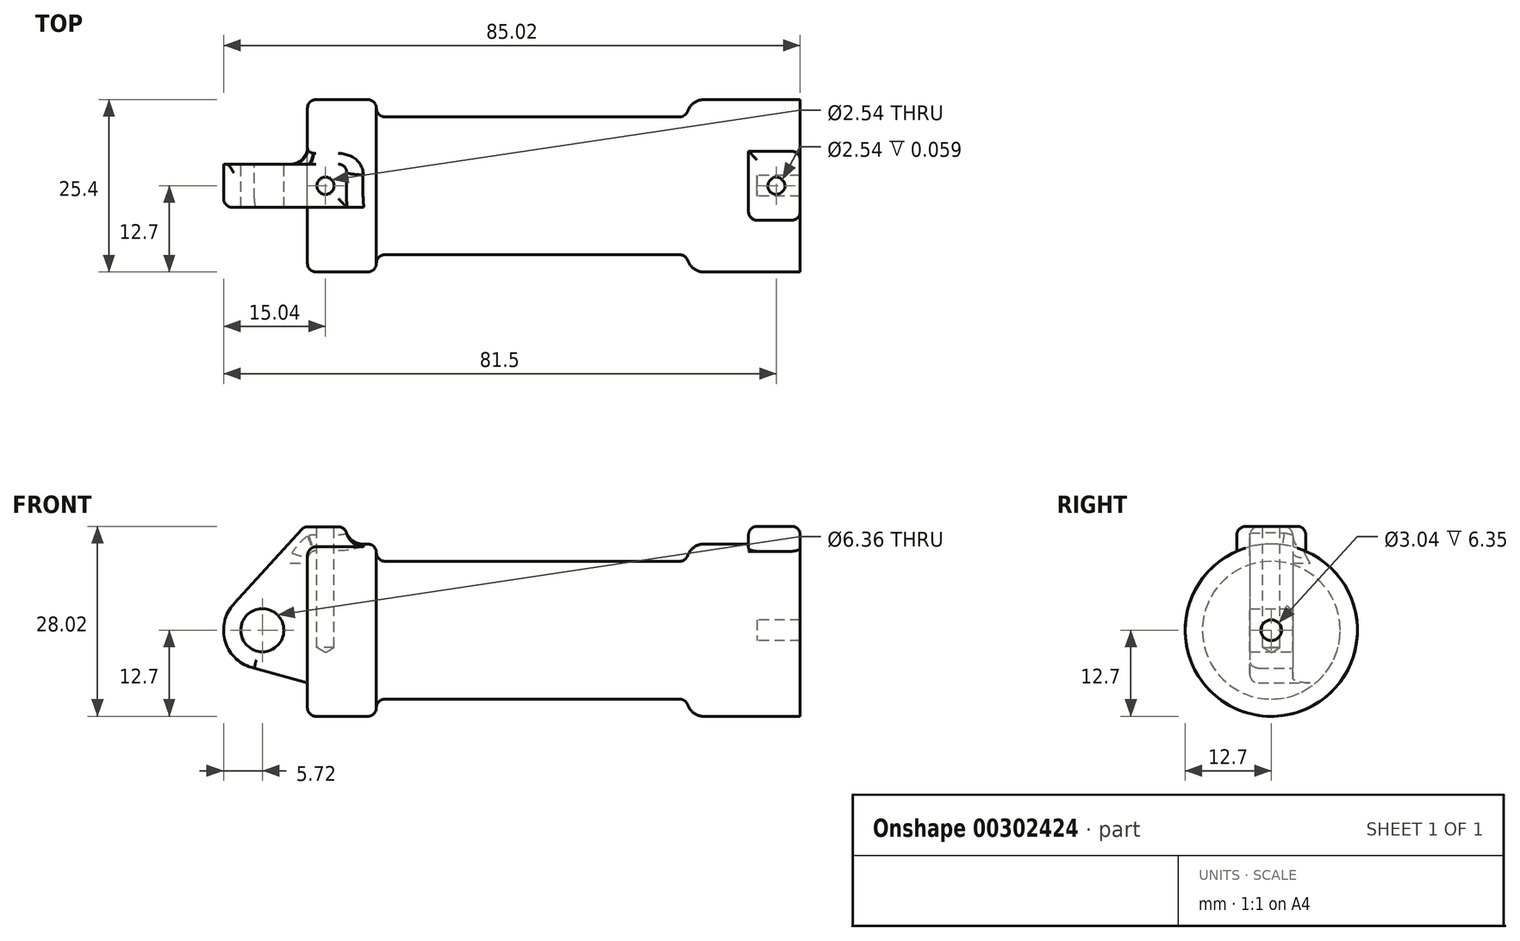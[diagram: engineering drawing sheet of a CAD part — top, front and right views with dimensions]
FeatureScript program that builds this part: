
annotation { "Feature Type Name" : "Feature", "Feature Type Description" : "" }
export const myFeature = defineFeature(function(context is Context, id is Id, definition is map)
    precondition{}
    {
        {
            var Q0;
            Q0=qCreatedBy(makeId("Front.planeOp"),FACE);
            var sketch = newSketch(context, id + "F0", { "sketchPlane" : qUnion([Q0])});
            skLineSegment(sketch, "E0", {"start": v(0, 0) * mm, "end": v(0, 12.7) * mm});
            skLineSegment(sketch, "E1", {"start": v(0, 12.7) * mm, "end": v(10.16, 12.7) * mm});
            skLineSegment(sketch, "E2", {"start": v(10.16, 12.7) * mm, "end": v(10.16, 10.16) * mm});
            skLineSegment(sketch, "E3", {"start": v(10.16, 10.16) * mm, "end": v(56.13, 10.16) * mm});
            skLineSegment(sketch, "E4", {"start": v(56.13, 10.16) * mm, "end": v(56.13, 12.7) * mm});
            skLineSegment(sketch, "E5", {"start": v(56.13, 12.7) * mm, "end": v(66.3, 12.7) * mm});
            skLineSegment(sketch, "E6", {"start": v(66.3, 12.7) * mm, "end": v(66.3, 0) * mm});
            skLineSegment(sketch, "E7", {"start": v(66.3, 0) * mm, "end": v(0, 0) * mm});
            skLineSegment(sketch, "E8", {"start": v(5.84, 15.24) * mm, "end": v(-0.5, 15.24) * mm});
            skLineSegment(sketch, "E9", {"start": v(-0.5, 15.24) * mm, "end": v(-10.88, 3.85) * mm});
            skLineSegment(sketch, "E10", {"start": v(0, 0) * mm, "end": v(-6.65, 0) * mm});
            skCircle(sketch, "E11", {"center": v(-6.65, 0) * mm, "radius": 5.72 * mm});
            skCircle(sketch, "E12", {"center": v(-6.65, 0) * mm, "radius": 3.18 * mm});
            skLineSegment(sketch, "E13", {"start": v(5.84, 15.24) * mm, "end": v(5.84, -9.4) * mm});
            skLineSegment(sketch, "E14", {"start": v(5.84, -9.4) * mm, "end": v(-8.18, -5.5) * mm});
            skSolve(sketch);
        }
        {
            var Q0;
            {var subQ0=sQuery(id+"F0.wireOp",EDGE,"E2");Q0=makeQuery(id+"F0.imprint","IMPRINT",FACE,{"disambiguationData":[TD([[makeQuery(id+"F0.imprint","IMPRINT",EDGE,{"derivedFrom":subQ0}),-1.0]])]});}
            var Q1;
            {var subQ0=sQuery(id+"F0.wireOp",EDGE,"E0");Q1=makeQuery(id+"F0.imprint","IMPRINT",FACE,{"disambiguationData":[TD([[makeQuery(id+"F0.imprint","IMPRINT",EDGE,{"derivedFrom":subQ0}),-1.0]])]});}
            var Q2;
            Q2=sQuery(id+"F0.wireOp",EDGE,"E7");
            revolve(context, id + "F1", {"entities" : qUnion([Q0, Q1]), "axis" : qUnion([Q2]), "revolveType" : RevolveType.FULL});
        }
        {
            var Q0;
            {var subQ1=sQuery(id+"F0.wireOp",EDGE,"E0");Q0=makeQuery(id+"F0.imprint","IMPRINT",FACE,{"disambiguationData":[TD([[makeQuery(id+"F0.imprint","IMPRINT",EDGE,{"derivedFrom":subQ1}),1.0]])]});}
            var Q1;
            {var subQ0=sQuery(id+"F0.wireOp",EDGE,"E14");Q1=makeQuery(id+"F0.imprint","IMPRINT",FACE,{"disambiguationData":[TD([[makeQuery(id+"F0.imprint","IMPRINT",EDGE,{"derivedFrom":subQ0}),-1.0]])]});}
            var Q2;
            {var subQ5=sQuery(id+"F0.wireOp",EDGE,"E12");Q2=makeQuery(id+"F0.imprint","IMPRINT",FACE,{"disambiguationData":[TD([[makeQuery(id+"F0.imprint","IMPRINT",EDGE,{"derivedFrom":subQ5}),-1.0]])]});}
            var Q3;
            {var subQ0=sQuery(id+"F0.wireOp",EDGE,"E0");Q3=makeQuery(id+"F0.imprint","IMPRINT",FACE,{"disambiguationData":[TD([[makeQuery(id+"F0.imprint","IMPRINT",EDGE,{"derivedFrom":subQ0}),-1.0]])]});}
            extrude(context, id + "F2", {"entities" : qUnion([Q0, Q1, Q2, Q3]), "operationType" : NewBodyOperationType.ADD, "depth" : 6.35 * mm, "symmetric" : true});
        }
        {
            var Q0;
            Q0=makeQuery(id+"F1.opRevolve","SWEPT_FACE",FACE,{"disambiguationData":[OSD([sQuery(id+"F0.wireOp",EDGE,"E6")])]});
            var sketch = newSketch(context, id + "F3", { "sketchPlane" : qUnion([Q0])});
            skCircle(sketch, "E15", {"center": v(0, 0) * mm, "radius": 5.08 * mm});
            skCircle(sketch, "E16", {"center": v(0, 0) * mm, "radius": 1.52 * mm});
            skLineSegment(sketch, "E17", {"start": v(-5.08, 0.16) * mm, "end": v(-5.08, 15.28) * mm});
            skLineSegment(sketch, "E18", {"start": v(5.08, 0) * mm, "end": v(5.08, 15.33) * mm});
            skLineSegment(sketch, "E19", {"start": v(5.08, 15.33) * mm, "end": v(-5.08, 15.28) * mm});
            skSolve(sketch);
        }
        {
            var Q0;
            {var subQ0=sQuery(id+"F3.wireOp",EDGE,"E19");Q0=makeQuery(id+"F3.imprint","IMPRINT",FACE,{"disambiguationData":[TD([[makeQuery(id+"F3.imprint","IMPRINT",EDGE,{"derivedFrom":subQ0}),1.0]])]});}
            var Q1;
            {var subQ0=sQuery(id+"F3.wireOp",EDGE,"E17");var subQ1=sQuery(id+"F3.wireOp",EDGE,"E15");var subQ2=makeQuery(id+"F3.imprint","INTERSECT",VERTEX,{"derivedFrom":[subQ1,subQ0]});Q1=makeQuery(id+"F3.imprint","IMPRINT",FACE,{"disambiguationData":[TD([[makeQuery(id+"F3.imprint","IMPRINT",EDGE,{"disambiguationData":[TD([[subQ2,1.0]])],"derivedFrom":subQ1}),-1.0]])]});}
            var Q2;
            Q2=makeQuery(id+"F3.imprint","IMPRINT",FACE,{"disambiguationData":[TD([[makeQuery(id+"F3.imprint","IMPRINT",EDGE,{"derivedFrom":sQuery(id+"F3.wireOp",EDGE,"E16")}),-1.0]])]});
            extrude(context, id + "F4", {"entities" : qUnion([Q0, Q1, Q2]), "operationType" : NewBodyOperationType.ADD, "depth" : 6.35 * mm, "hasSecondDirection" : true, "secondDirectionOppositeDirection" : true, "secondDirectionDepth" : 1.27 * mm});
        }
        {
            var Q0;
            Q0=makeQuery(id+"F2.opExtrude","SWEPT_FACE",FACE,{"disambiguationData":[OSD([sQuery(id+"F0.wireOp",EDGE,"E8")])]});
            var sketch = newSketch(context, id + "F5", { "sketchPlane" : qUnion([Q0])});
            skCircle(sketch, "E20", {"center": v(2.67, 0) * mm, "radius": 1.52 * mm});
            skCircle(sketch, "E21", {"center": v(69.13, 0) * mm, "radius": 1.52 * mm});
            skSolve(sketch);
        }
        {
            var Q0;
            Q0=makeQuery(id+"F1.opRevolve","SWEPT_EDGE",EDGE,{"disambiguationData":[OSD([sQuery(id+"F0.wireOp",EDGE,"E0"),sQuery(id+"F0.wireOp",EDGE,"E1")])]});
            var Q1;
            Q1=makeQuery(id+"F1.opRevolve","SWEPT_EDGE",EDGE,{"disambiguationData":[OSD([sQuery(id+"F0.wireOp",EDGE,"E5"),sQuery(id+"F0.wireOp",EDGE,"E6")])]});
            var Q2;
            Q2=makeQuery(id+"F1.opRevolve","SWEPT_EDGE",EDGE,{"disambiguationData":[OSD([sQuery(id+"F0.wireOp",EDGE,"E1"),sQuery(id+"F0.wireOp",EDGE,"E2")])]});
            var Q3;
            Q3=makeQuery(id+"F1.opRevolve","SWEPT_FACE",FACE,{"disambiguationData":[OSD([sQuery(id+"F0.wireOp",EDGE,"E3")])]});
            var Q4;
            Q4=makeQuery(id+"F2.opExtrude","CAP_EDGE",EDGE,{"disambiguationData":[OSD([sQuery(id+"F0.wireOp",EDGE,"E8")])],"isStart":false});
            var Q5;
            {var subQ0=sQuery(id+"F0.wireOp",EDGE,"E13");Q5=makeQuery(id+"F2.opExtrude","CAP_EDGE",EDGE,{"disambiguationData":[OSD([subQ0]),TDD([makeQuery(id+"F0.imprint","IMPRINT",EDGE,{"disambiguationData":[TD([[makeQuery(id+"F0.imprint","INTERSECT",VERTEX,{"derivedFrom":[sQuery(id+"F0.wireOp",EDGE,"E8"),subQ0]}),-1.0]])],"derivedFrom":subQ0})])],"isStart":true});}
            var Q6;
            Q6=makeQuery(id+"F2.opExtrude","SWEPT_EDGE",EDGE,{"disambiguationData":[OSD([sQuery(id+"F0.wireOp",EDGE,"E1"),sQuery(id+"F0.wireOp",EDGE,"E13")])]});
            var Q7;
            Q7=makeQuery(id+"F2.opExtrude","SWEPT_EDGE",EDGE,{"disambiguationData":[OSD([sQuery(id+"F0.wireOp",EDGE,"E8"),sQuery(id+"F0.wireOp",EDGE,"E13")])]});
            var Q8;
            Q8=makeQuery(id+"F2.opExtrude","CAP_EDGE",EDGE,{"disambiguationData":[OSD([sQuery(id+"F0.wireOp",EDGE,"E9")])],"isStart":false});
            var Q9;
            Q9=makeQuery(id+"F2.opExtrude","CAP_EDGE",EDGE,{"disambiguationData":[OSD([sQuery(id+"F0.wireOp",EDGE,"E11")])],"isStart":false});
            var Q10;
            Q10=makeQuery(id+"F2.opExtrude","SWEPT_EDGE",EDGE,{"disambiguationData":[OSD([sQuery(id+"F0.wireOp",EDGE,"E8"),sQuery(id+"F0.wireOp",EDGE,"E9")])]});
            var Q11;
            Q11=makeQuery(id+"F2.opExtrude","CAP_EDGE",EDGE,{"disambiguationData":[OSD([sQuery(id+"F0.wireOp",EDGE,"E8")])],"isStart":true});
            var Q12;
            Q12=makeQuery(id+"F2.opExtrude","CAP_EDGE",EDGE,{"disambiguationData":[OSD([sQuery(id+"F0.wireOp",EDGE,"E9")])],"isStart":true});
            var Q13;
            Q13=makeQuery(id+"F2.opExtrude","SWEPT_EDGE",EDGE,{"disambiguationData":[OSD([sQuery(id+"F0.wireOp",EDGE,"E9"),sQuery(id+"F0.wireOp",EDGE,"E11")])]});
            var Q14;
            Q14=makeQuery(id+"F4.opExtrude","CAP_EDGE",EDGE,{"disambiguationData":[OSD([sQuery(id+"F3.wireOp",EDGE,"E19")])],"isStart":false});
            var Q15;
            Q15=makeQuery(id+"F4.opExtrude","CAP_EDGE",EDGE,{"disambiguationData":[OSD([sQuery(id+"F3.wireOp",EDGE,"E17")])],"isStart":false});
            var Q16;
            Q16=makeQuery(id+"F4.opExtrude","CAP_EDGE",EDGE,{"disambiguationData":[OSD([sQuery(id+"F3.wireOp",EDGE,"E15")])],"isStart":false});
            var Q17;
            Q17=makeQuery(id+"F4.boolean.opBoolean","INTERSECT",EDGE,{"derivedFrom":[makeQuery(id+"F1.opRevolve","SWEPT_FACE",FACE,{"disambiguationData":[OSD([sQuery(id+"F0.wireOp",EDGE,"E6")])]}),makeQuery(id+"F4.opExtrude","SWEPT_FACE",FACE,{"disambiguationData":[OSD([sQuery(id+"F3.wireOp",EDGE,"E17")])]})]});
            var Q18;
            Q18=makeQuery(id+"F4.opExtrude","CAP_EDGE",EDGE,{"disambiguationData":[OSD([sQuery(id+"F3.wireOp",EDGE,"E17")])],"isStart":true});
            var Q19;
            Q19=makeQuery(id+"F4.opExtrude","CAP_EDGE",EDGE,{"disambiguationData":[OSD([sQuery(id+"F3.wireOp",EDGE,"E19")])],"isStart":true});
            var Q20;
            Q20=makeQuery(id+"F4.opExtrude","SWEPT_EDGE",EDGE,{"disambiguationData":[OSD([sQuery(id+"F3.wireOp",EDGE,"E18"),sQuery(id+"F3.wireOp",EDGE,"E19")])]});
            var Q21;
            Q21=makeQuery(id+"F4.opExtrude","SWEPT_EDGE",EDGE,{"disambiguationData":[OSD([sQuery(id+"F3.wireOp",EDGE,"E17"),sQuery(id+"F3.wireOp",EDGE,"E19")])]});
            var Q22;
            Q22=makeQuery(id+"F4.boolean.opBoolean","INTERSECT",EDGE,{"derivedFrom":[makeQuery(id+"F1.opRevolve","SWEPT_FACE",FACE,{"disambiguationData":[OSD([sQuery(id+"F0.wireOp",EDGE,"E5")])]}),makeQuery(id+"F4.opExtrude","SWEPT_FACE",FACE,{"disambiguationData":[OSD([sQuery(id+"F3.wireOp",EDGE,"E17")])]})]});
            var Q23;
            Q23=makeQuery(id+"F4.opExtrude","CAP_EDGE",EDGE,{"disambiguationData":[OSD([sQuery(id+"F3.wireOp",EDGE,"E18")])],"isStart":false});
            fillet(context, id + "F6", {"entities" : qUnion([Q0, Q1, Q2, Q3, Q4, Q5, Q6, Q7, Q8, Q9, Q10, Q11, Q12, Q13, Q14, Q15, Q16, Q17, Q18, Q19, Q20, Q21, Q22, Q23]), "radius" : 1.27 * mm, "tangentPropagation" : true, "allowEdgeOverflow" : false});
        }
        {
            var Q0;
            Q0=sQuery(id+"F5.wireOp",VERTEX,"E20.center");
            var Q1;
            Q1=makeQuery(id+"F1.opRevolve","SWEPT_BODY",BODY,{"disambiguationData":[OSD([sQuery(id+"F0.wireOp",EDGE,"E0"),sQuery(id+"F0.wireOp",EDGE,"E1"),sQuery(id+"F0.wireOp",EDGE,"E2"),sQuery(id+"F0.wireOp",EDGE,"E3"),sQuery(id+"F0.wireOp",EDGE,"E4"),sQuery(id+"F0.wireOp",EDGE,"E5"),sQuery(id+"F0.wireOp",EDGE,"E6"),sQuery(id+"F0.wireOp",EDGE,"E7")])]});
            var Q2;
            Q2=makeQuery(id+"F2.opExtrude","SWEPT_BODY",BODY,{"disambiguationData":[OSD([sQuery(id+"F0.wireOp",EDGE,"E0"),sQuery(id+"F0.wireOp",EDGE,"E1"),sQuery(id+"F0.wireOp",EDGE,"E7"),sQuery(id+"F0.wireOp",EDGE,"E8"),sQuery(id+"F0.wireOp",EDGE,"E9"),sQuery(id+"F0.wireOp",EDGE,"E11"),sQuery(id+"F0.wireOp",EDGE,"E12"),sQuery(id+"F0.wireOp",EDGE,"E13"),sQuery(id+"F0.wireOp",EDGE,"E14")])]});
            hole(context, id + "F7", {"style" : HoleStyle.SIMPLE, "endStyle" : HoleEndStyle.BLIND, "holeDiameter" : 2.54 * mm, "holeDepth" : 17.78 * mm, "tappedDepth" : 12.7 * mm, "tapClearance" : 3, "locations" : qUnion([Q0]), "scope" : qUnion([Q1, Q2])});
        }
        {
            var Q0;
            Q0=sQuery(id+"F5.wireOp",VERTEX,"E21.center");
            var Q1;
            Q1=makeQuery(id+"F1.opRevolve","SWEPT_BODY",BODY,{"disambiguationData":[OSD([sQuery(id+"F0.wireOp",EDGE,"E0"),sQuery(id+"F0.wireOp",EDGE,"E1"),sQuery(id+"F0.wireOp",EDGE,"E2"),sQuery(id+"F0.wireOp",EDGE,"E3"),sQuery(id+"F0.wireOp",EDGE,"E4"),sQuery(id+"F0.wireOp",EDGE,"E5"),sQuery(id+"F0.wireOp",EDGE,"E6"),sQuery(id+"F0.wireOp",EDGE,"E7")])]});
            hole(context, id + "F8", {"style" : HoleStyle.SIMPLE, "endStyle" : HoleEndStyle.BLIND, "oppositeDirection" : true, "holeDiameter" : 2.54 * mm, "holeDepth" : 10.4 * mm, "tappedDepth" : 12.7 * mm, "tapClearance" : 3, "locations" : qUnion([Q0]), "scope" : qUnion([Q1])});
        }
        {
            var Q0;
            Q0=makeQuery(id+"F1.opRevolve","SWEPT_EDGE",EDGE,{"disambiguationData":[OSD([sQuery(id+"F0.wireOp",EDGE,"E4"),sQuery(id+"F0.wireOp",EDGE,"E5")])]});
            fillet(context, id + "F9", {"entities" : qUnion([Q0]), "radius" : 2.54 * mm, "tangentPropagation" : true, "allowEdgeOverflow" : false});
        }
        {
            var Q0;
            Q0=makeQuery(id+"F6.opFillet","BLEND_EDGE",EDGE,{"blendedFrom":[makeQuery(id+"F2.opExtrude","CAP_EDGE",EDGE,{"disambiguationData":[OSD([sQuery(id+"F0.wireOp",EDGE,"E13")])],"isStart":true}),makeQuery(id+"F1.opRevolve","SWEPT_FACE",FACE,{"disambiguationData":[OSD([sQuery(id+"F0.wireOp",EDGE,"E1")])]})],"blendedInto":[makeQuery(id+"F1.opRevolve","SWEPT_FACE",FACE,{"disambiguationData":[OSD([sQuery(id+"F0.wireOp",EDGE,"E1")])]})]});
            fillet(context, id + "F10", {"entities" : qUnion([Q0]), "radius" : 2.54 * mm, "tangentPropagation" : true, "allowEdgeOverflow" : false});
        }
    });
